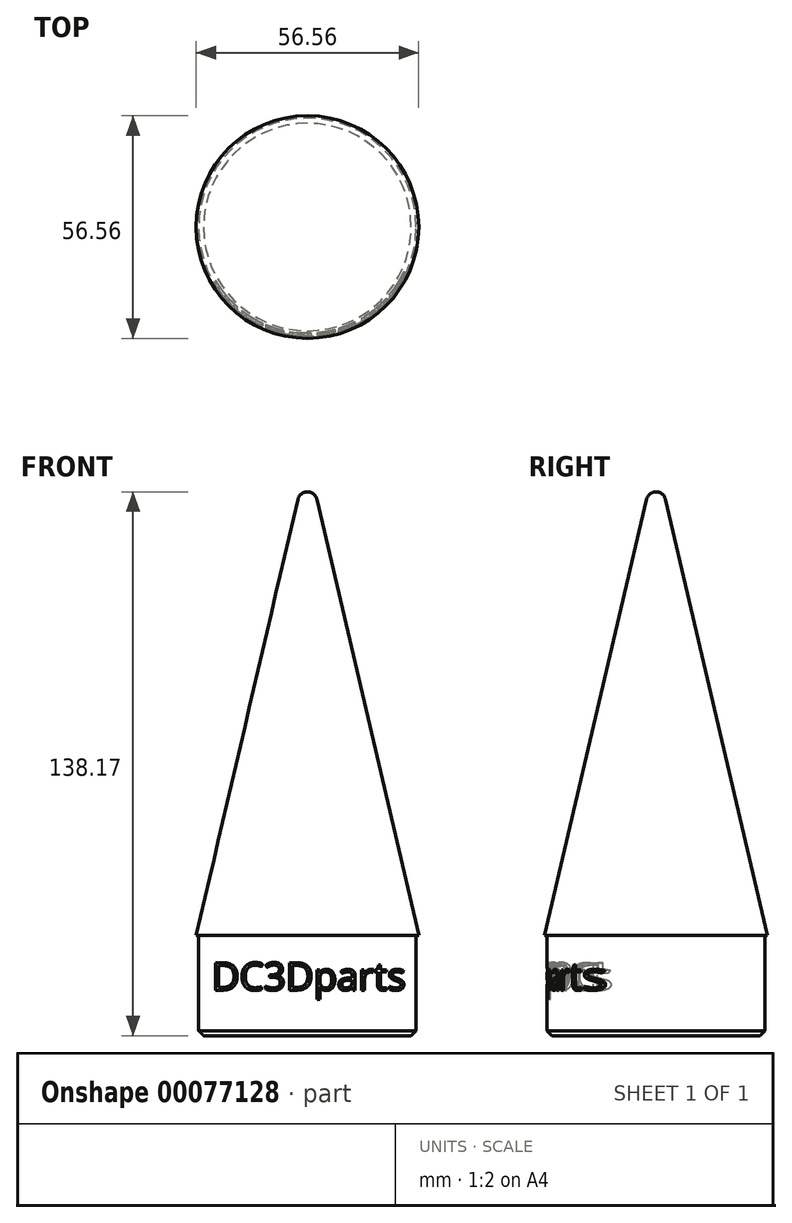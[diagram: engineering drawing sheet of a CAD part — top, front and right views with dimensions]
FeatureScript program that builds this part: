
annotation { "Feature Type Name" : "Feature", "Feature Type Description" : "" }
export const myFeature = defineFeature(function(context is Context, id is Id, definition is map)
    precondition{}
    {
        {
            var Q0;
            Q0=qCreatedBy(makeId("Front.planeOp"),FACE);
            var sketch = newSketch(context, id + "F0", { "sketchPlane" : qUnion([Q0])});
            skLineSegment(sketch, "E0", {"start": v(-33.35, -68.75) * mm, "end": v(-32.6, -68.75) * mm});
            skLineSegment(sketch, "E1", {"start": v(0, -68.75) * mm, "end": v(0, 86.96) * mm});
            skLineSegment(sketch, "E2", {"start": v(0, -68.75) * mm, "end": v(0, -98.75) * mm});
            skLineSegment(sketch, "E3", {"start": v(0, -98.75) * mm, "end": v(-32.6, -98.75) * mm});
            skLineSegment(sketch, "E4", {"start": v(-32.6, -98.75) * mm, "end": v(-32.6, -68.75) * mm});
            skLineSegment(sketch, "E5.trimOffspring", {"start": v(-32.6, -68.75) * mm, "end": v(-33.35, -68.75) * mm});
            skPoint(sketch, "E6.orphan", {"position": v(0, 61.25) * mm});
            skLineSegment(sketch, "E7", {"start": v(-33.35, -68.75) * mm, "end": v(-2.86, 61.92) * mm});
            skArc(sketch, "E8", {"start": v(0, 64.19) * mm, "mid": v(-1.82, 63.55) * mm, "end": v(-2.86, 61.92) * mm});
            skSolve(sketch);
        }
        {
            var Q0;
            {var subQ0=sQuery(id+"F0.wireOp",EDGE,"E2");Q0=makeQuery(id+"F0.imprint","IMPRINT",FACE,{"disambiguationData":[TD([[makeQuery(id+"F0.imprint","IMPRINT",EDGE,{"derivedFrom":subQ0}),-1.0]])]});}
            var Q1;
            Q1=sQuery(id+"F0.wireOp",EDGE,"E1");
            revolve(context, id + "F1", {"entities" : qUnion([Q0]), "axis" : qUnion([Q1]), "revolveType" : RevolveType.FULL});
        }
        {
            var Q0;
            Q0=makeQuery(id+"F1.opRevolve","SWEPT_EDGE",EDGE,{"disambiguationData":[OSD([sQuery(id+"F0.wireOp",EDGE,"E3"),sQuery(id+"F0.wireOp",EDGE,"E4")])]});
            chamfer(context, id + "F2", {"entities" : qUnion([Q0]), "width" : 1.5 * mm, "tangentPropagation" : true});
        }
        {
            var Q0;
            Q0=makeQuery(id+"F1.opRevolve","SWEPT_BODY",BODY,{"disambiguationData":[OSD([sQuery(id+"F0.wireOp",EDGE,"Oh61cgLR-RQo2-T4aV-TcRg-Gp7ijPdUG9jl"),sQuery(id+"F0.wireOp",EDGE,"E1"),sQuery(id+"F0.wireOp",EDGE,"E2"),sQuery(id+"F0.wireOp",EDGE,"E3"),sQuery(id+"F0.wireOp",EDGE,"E4"),sQuery(id+"F0.wireOp",EDGE,"E5.trimOffspring"),sQuery(id+"F0.wireOp",EDGE,"dTV1AxgJ-VMAe-DLQO-Zqz3-4UbtDb8FiUJC")])]});
            var Q1;
            Q1=qCreatedBy(makeId("Origin.pointOp"),VERTEX);
            transform(context, id + "F3", {"entities" : qUnion([Q0]), "transformType" : TransformType.SCALE_UNIFORMLY, "scale" : .848, "scalePoint" : qUnion([Q1]), "makeCopy" : false});
        }
        {
            var Q0;
            Q0=qCreatedBy(makeId("Front.planeOp"),FACE);
            cPlane(context, id + "F4", {"entities" : qUnion([Q0]), "cplaneType" : CPlaneType.OFFSET, "offset" : 35 * mm, "width" : 150 * mm, "height" : 150 * mm});
        }
        {
            var Q0;
            Q0=qCreatedBy(makeId("Front.planeOp"),FACE);
            var sketch = newSketch(context, id + "F5", { "sketchPlane" : qUnion([Q0])});
            skLineSegment(sketch, "E9.bottom", {"start": v(0, -61.28) * mm, "end": v(-27, -61.28) * mm});
            skLineSegment(sketch, "E9.top", {"start": v(0, -97.48) * mm, "end": v(-27, -97.48) * mm});
            skLineSegment(sketch, "E9.left", {"start": v(0, -61.28) * mm, "end": v(0, -97.48) * mm});
            skLineSegment(sketch, "E9.right", {"start": v(-27, -61.28) * mm, "end": v(-27, -97.48) * mm});
            skSolve(sketch);
        }
        {
            var Q0;
            Q0=makeQuery(id+"F5.imprint","IMPRINT",FACE,{"disambiguationData":[TD([[makeQuery(id+"F5.imprint","IMPRINT",EDGE,{"derivedFrom":sQuery(id+"F5.wireOp",EDGE,"E9.bottom")}),1.0]])]});
            var Q1;
            Q1=sQuery(id+"F5.wireOp",EDGE,"E9.left");
            revolve(context, id + "F6", {"entities" : qUnion([Q0]), "axis" : qUnion([Q1]), "revolveType" : RevolveType.FULL});
        }
        {
            var Q0;
            Q0=qCreatedBy(id+"F4.planeOp",FACE);
            var sketch = newSketch(context, id + "F7", { "sketchPlane" : qUnion([Q0])});
            skText(sketch, "E10", { "text": "DC3Dparts", "fontName": "OpenSans-Regular.ttf"});
            const initialGuessF7  = {"E10": [-0.02432, -0.07217, 1, 0, 0.007]};
            skSetInitialGuess(sketch, initialGuessF7);
            skSolve(sketch);
        }
        {
            var Q0;
            Q0 = qSketchRegion(id + "F7", true);
            var Q1;
            Q1=qCreatedBy(makeId("Front.planeOp"),FACE);
            extrude(context, id + "F8", {"entities" : qUnion([Q0]), "endBound" : BoundingType.UP_TO_SURFACE, "oppositeDirection" : true, "depth" : 25 * mm, "endBoundEntityFace" : qUnion([Q1]), "offsetDistance" : 25 * mm});
        }
        {
            var Q0;
            Q0=makeQuery(id+"F6.opRevolve","SWEPT_BODY",BODY,{"disambiguationData":[OSD([sQuery(id+"F5.wireOp",EDGE,"E9.bottom"),sQuery(id+"F5.wireOp",EDGE,"E9.top"),sQuery(id+"F5.wireOp",EDGE,"E9.left"),sQuery(id+"F5.wireOp",EDGE,"E9.right")])]});
            var Q1;
            Q1=makeQuery(id+"F8.opExtrude","SWEPT_BODY",BODY,{"disambiguationData":[OSD([sQuery(id+"F7.wireOp",EDGE,"E10.sketch_text.stroke-0"),sQuery(id+"F7.wireOp",EDGE,"E10.sketch_text.stroke-1"),sQuery(id+"F7.wireOp",EDGE,"E10.sketch_text.stroke-2"),sQuery(id+"F7.wireOp",EDGE,"E10.sketch_text.stroke-3"),sQuery(id+"F7.wireOp",EDGE,"E10.sketch_text.stroke-4"),sQuery(id+"F7.wireOp",EDGE,"E10.sketch_text.stroke-5"),sQuery(id+"F7.wireOp",EDGE,"E10.sketch_text.stroke-6"),sQuery(id+"F7.wireOp",EDGE,"E10.sketch_text.stroke-7"),sQuery(id+"F7.wireOp",EDGE,"E10.sketch_text.stroke-8"),sQuery(id+"F7.wireOp",EDGE,"E10.sketch_text.stroke-9"),sQuery(id+"F7.wireOp",EDGE,"E10.sketch_text.stroke-10"),sQuery(id+"F7.wireOp",EDGE,"E10.sketch_text.stroke-11"),sQuery(id+"F7.wireOp",EDGE,"E10.sketch_text.stroke-12"),sQuery(id+"F7.wireOp",EDGE,"E10.sketch_text.stroke-13")])]});
            var Q2;
            Q2=makeQuery(id+"F8.opExtrude","SWEPT_BODY",BODY,{"disambiguationData":[OSD([sQuery(id+"F7.wireOp",EDGE,"E10.sketch_text.stroke-14"),sQuery(id+"F7.wireOp",EDGE,"E10.sketch_text.stroke-15"),sQuery(id+"F7.wireOp",EDGE,"E10.sketch_text.stroke-16"),sQuery(id+"F7.wireOp",EDGE,"E10.sketch_text.stroke-17"),sQuery(id+"F7.wireOp",EDGE,"E10.sketch_text.stroke-18"),sQuery(id+"F7.wireOp",EDGE,"E10.sketch_text.stroke-19"),sQuery(id+"F7.wireOp",EDGE,"E10.sketch_text.stroke-20"),sQuery(id+"F7.wireOp",EDGE,"E10.sketch_text.stroke-21"),sQuery(id+"F7.wireOp",EDGE,"E10.sketch_text.stroke-22"),sQuery(id+"F7.wireOp",EDGE,"E10.sketch_text.stroke-23"),sQuery(id+"F7.wireOp",EDGE,"E10.sketch_text.stroke-24"),sQuery(id+"F7.wireOp",EDGE,"E10.sketch_text.stroke-25"),sQuery(id+"F7.wireOp",EDGE,"E10.sketch_text.stroke-26"),sQuery(id+"F7.wireOp",EDGE,"E10.sketch_text.stroke-27"),sQuery(id+"F7.wireOp",EDGE,"E10.sketch_text.stroke-28")])]});
            var Q3;
            Q3=makeQuery(id+"F8.opExtrude","SWEPT_BODY",BODY,{"disambiguationData":[OSD([sQuery(id+"F7.wireOp",EDGE,"E10.sketch_text.stroke-29"),sQuery(id+"F7.wireOp",EDGE,"E10.sketch_text.stroke-30"),sQuery(id+"F7.wireOp",EDGE,"E10.sketch_text.stroke-31"),sQuery(id+"F7.wireOp",EDGE,"E10.sketch_text.stroke-32"),sQuery(id+"F7.wireOp",EDGE,"E10.sketch_text.stroke-33"),sQuery(id+"F7.wireOp",EDGE,"E10.sketch_text.stroke-34"),sQuery(id+"F7.wireOp",EDGE,"E10.sketch_text.stroke-35"),sQuery(id+"F7.wireOp",EDGE,"E10.sketch_text.stroke-36"),sQuery(id+"F7.wireOp",EDGE,"E10.sketch_text.stroke-37"),sQuery(id+"F7.wireOp",EDGE,"E10.sketch_text.stroke-38"),sQuery(id+"F7.wireOp",EDGE,"E10.sketch_text.stroke-39"),sQuery(id+"F7.wireOp",EDGE,"E10.sketch_text.stroke-40"),sQuery(id+"F7.wireOp",EDGE,"E10.sketch_text.stroke-41"),sQuery(id+"F7.wireOp",EDGE,"E10.sketch_text.stroke-42"),sQuery(id+"F7.wireOp",EDGE,"E10.sketch_text.stroke-43"),sQuery(id+"F7.wireOp",EDGE,"E10.sketch_text.stroke-44"),sQuery(id+"F7.wireOp",EDGE,"E10.sketch_text.stroke-45"),sQuery(id+"F7.wireOp",EDGE,"E10.sketch_text.stroke-46"),sQuery(id+"F7.wireOp",EDGE,"E10.sketch_text.stroke-47"),sQuery(id+"F7.wireOp",EDGE,"E10.sketch_text.stroke-48"),sQuery(id+"F7.wireOp",EDGE,"E10.sketch_text.stroke-49"),sQuery(id+"F7.wireOp",EDGE,"E10.sketch_text.stroke-50"),sQuery(id+"F7.wireOp",EDGE,"E10.sketch_text.stroke-51"),sQuery(id+"F7.wireOp",EDGE,"E10.sketch_text.stroke-52"),sQuery(id+"F7.wireOp",EDGE,"E10.sketch_text.stroke-53"),sQuery(id+"F7.wireOp",EDGE,"E10.sketch_text.stroke-54"),sQuery(id+"F7.wireOp",EDGE,"E10.sketch_text.stroke-55"),sQuery(id+"F7.wireOp",EDGE,"E10.sketch_text.stroke-56")])]});
            var Q4;
            Q4=makeQuery(id+"F8.opExtrude","SWEPT_BODY",BODY,{"disambiguationData":[OSD([sQuery(id+"F7.wireOp",EDGE,"E10.sketch_text.stroke-57"),sQuery(id+"F7.wireOp",EDGE,"E10.sketch_text.stroke-58"),sQuery(id+"F7.wireOp",EDGE,"E10.sketch_text.stroke-59"),sQuery(id+"F7.wireOp",EDGE,"E10.sketch_text.stroke-60"),sQuery(id+"F7.wireOp",EDGE,"E10.sketch_text.stroke-61"),sQuery(id+"F7.wireOp",EDGE,"E10.sketch_text.stroke-62"),sQuery(id+"F7.wireOp",EDGE,"E10.sketch_text.stroke-63"),sQuery(id+"F7.wireOp",EDGE,"E10.sketch_text.stroke-64"),sQuery(id+"F7.wireOp",EDGE,"E10.sketch_text.stroke-65"),sQuery(id+"F7.wireOp",EDGE,"E10.sketch_text.stroke-66"),sQuery(id+"F7.wireOp",EDGE,"E10.sketch_text.stroke-67"),sQuery(id+"F7.wireOp",EDGE,"E10.sketch_text.stroke-68"),sQuery(id+"F7.wireOp",EDGE,"E10.sketch_text.stroke-69"),sQuery(id+"F7.wireOp",EDGE,"E10.sketch_text.stroke-70")])]});
            var Q5;
            Q5=makeQuery(id+"F8.opExtrude","SWEPT_BODY",BODY,{"disambiguationData":[OSD([sQuery(id+"F7.wireOp",EDGE,"E10.sketch_text.stroke-71"),sQuery(id+"F7.wireOp",EDGE,"E10.sketch_text.stroke-72"),sQuery(id+"F7.wireOp",EDGE,"E10.sketch_text.stroke-73"),sQuery(id+"F7.wireOp",EDGE,"E10.sketch_text.stroke-74"),sQuery(id+"F7.wireOp",EDGE,"E10.sketch_text.stroke-75"),sQuery(id+"F7.wireOp",EDGE,"E10.sketch_text.stroke-76"),sQuery(id+"F7.wireOp",EDGE,"E10.sketch_text.stroke-77"),sQuery(id+"F7.wireOp",EDGE,"E10.sketch_text.stroke-78"),sQuery(id+"F7.wireOp",EDGE,"E10.sketch_text.stroke-79"),sQuery(id+"F7.wireOp",EDGE,"E10.sketch_text.stroke-80"),sQuery(id+"F7.wireOp",EDGE,"E10.sketch_text.stroke-81"),sQuery(id+"F7.wireOp",EDGE,"E10.sketch_text.stroke-82"),sQuery(id+"F7.wireOp",EDGE,"E10.sketch_text.stroke-83"),sQuery(id+"F7.wireOp",EDGE,"E10.sketch_text.stroke-84"),sQuery(id+"F7.wireOp",EDGE,"E10.sketch_text.stroke-85"),sQuery(id+"F7.wireOp",EDGE,"E10.sketch_text.stroke-86"),sQuery(id+"F7.wireOp",EDGE,"E10.sketch_text.stroke-87"),sQuery(id+"F7.wireOp",EDGE,"E10.sketch_text.stroke-88"),sQuery(id+"F7.wireOp",EDGE,"E10.sketch_text.stroke-89"),sQuery(id+"F7.wireOp",EDGE,"E10.sketch_text.stroke-90"),sQuery(id+"F7.wireOp",EDGE,"E10.sketch_text.stroke-91"),sQuery(id+"F7.wireOp",EDGE,"E10.sketch_text.stroke-92"),sQuery(id+"F7.wireOp",EDGE,"E10.sketch_text.stroke-93"),sQuery(id+"F7.wireOp",EDGE,"E10.sketch_text.stroke-94"),sQuery(id+"F7.wireOp",EDGE,"E10.sketch_text.stroke-95")])]});
            var Q6;
            Q6=makeQuery(id+"F8.opExtrude","SWEPT_BODY",BODY,{"disambiguationData":[OSD([sQuery(id+"F7.wireOp",EDGE,"E10.sketch_text.stroke-96"),sQuery(id+"F7.wireOp",EDGE,"E10.sketch_text.stroke-97"),sQuery(id+"F7.wireOp",EDGE,"E10.sketch_text.stroke-98"),sQuery(id+"F7.wireOp",EDGE,"E10.sketch_text.stroke-99"),sQuery(id+"F7.wireOp",EDGE,"E10.sketch_text.stroke-100"),sQuery(id+"F7.wireOp",EDGE,"E10.sketch_text.stroke-101"),sQuery(id+"F7.wireOp",EDGE,"E10.sketch_text.stroke-102"),sQuery(id+"F7.wireOp",EDGE,"E10.sketch_text.stroke-103"),sQuery(id+"F7.wireOp",EDGE,"E10.sketch_text.stroke-104"),sQuery(id+"F7.wireOp",EDGE,"E10.sketch_text.stroke-105"),sQuery(id+"F7.wireOp",EDGE,"E10.sketch_text.stroke-106"),sQuery(id+"F7.wireOp",EDGE,"E10.sketch_text.stroke-107"),sQuery(id+"F7.wireOp",EDGE,"E10.sketch_text.stroke-108"),sQuery(id+"F7.wireOp",EDGE,"E10.sketch_text.stroke-109"),sQuery(id+"F7.wireOp",EDGE,"E10.sketch_text.stroke-110"),sQuery(id+"F7.wireOp",EDGE,"E10.sketch_text.stroke-111"),sQuery(id+"F7.wireOp",EDGE,"E10.sketch_text.stroke-112"),sQuery(id+"F7.wireOp",EDGE,"E10.sketch_text.stroke-113"),sQuery(id+"F7.wireOp",EDGE,"E10.sketch_text.stroke-114"),sQuery(id+"F7.wireOp",EDGE,"E10.sketch_text.stroke-115"),sQuery(id+"F7.wireOp",EDGE,"E10.sketch_text.stroke-116"),sQuery(id+"F7.wireOp",EDGE,"E10.sketch_text.stroke-117"),sQuery(id+"F7.wireOp",EDGE,"E10.sketch_text.stroke-118"),sQuery(id+"F7.wireOp",EDGE,"E10.sketch_text.stroke-119"),sQuery(id+"F7.wireOp",EDGE,"E10.sketch_text.stroke-120"),sQuery(id+"F7.wireOp",EDGE,"E10.sketch_text.stroke-121"),sQuery(id+"F7.wireOp",EDGE,"E10.sketch_text.stroke-122")])]});
            var Q7;
            Q7=makeQuery(id+"F8.opExtrude","SWEPT_BODY",BODY,{"disambiguationData":[OSD([sQuery(id+"F7.wireOp",EDGE,"E10.sketch_text.stroke-123"),sQuery(id+"F7.wireOp",EDGE,"E10.sketch_text.stroke-124"),sQuery(id+"F7.wireOp",EDGE,"E10.sketch_text.stroke-125"),sQuery(id+"F7.wireOp",EDGE,"E10.sketch_text.stroke-126"),sQuery(id+"F7.wireOp",EDGE,"E10.sketch_text.stroke-127"),sQuery(id+"F7.wireOp",EDGE,"E10.sketch_text.stroke-128"),sQuery(id+"F7.wireOp",EDGE,"E10.sketch_text.stroke-129"),sQuery(id+"F7.wireOp",EDGE,"E10.sketch_text.stroke-130"),sQuery(id+"F7.wireOp",EDGE,"E10.sketch_text.stroke-131"),sQuery(id+"F7.wireOp",EDGE,"E10.sketch_text.stroke-132"),sQuery(id+"F7.wireOp",EDGE,"E10.sketch_text.stroke-133"),sQuery(id+"F7.wireOp",EDGE,"E10.sketch_text.stroke-134"),sQuery(id+"F7.wireOp",EDGE,"E10.sketch_text.stroke-135")])]});
            var Q8;
            Q8=makeQuery(id+"F8.opExtrude","SWEPT_BODY",BODY,{"disambiguationData":[OSD([sQuery(id+"F7.wireOp",EDGE,"E10.sketch_text.stroke-136"),sQuery(id+"F7.wireOp",EDGE,"E10.sketch_text.stroke-137"),sQuery(id+"F7.wireOp",EDGE,"E10.sketch_text.stroke-138"),sQuery(id+"F7.wireOp",EDGE,"E10.sketch_text.stroke-139"),sQuery(id+"F7.wireOp",EDGE,"E10.sketch_text.stroke-140"),sQuery(id+"F7.wireOp",EDGE,"E10.sketch_text.stroke-141"),sQuery(id+"F7.wireOp",EDGE,"E10.sketch_text.stroke-142"),sQuery(id+"F7.wireOp",EDGE,"E10.sketch_text.stroke-143"),sQuery(id+"F7.wireOp",EDGE,"E10.sketch_text.stroke-144"),sQuery(id+"F7.wireOp",EDGE,"E10.sketch_text.stroke-145"),sQuery(id+"F7.wireOp",EDGE,"E10.sketch_text.stroke-146"),sQuery(id+"F7.wireOp",EDGE,"E10.sketch_text.stroke-147"),sQuery(id+"F7.wireOp",EDGE,"E10.sketch_text.stroke-148"),sQuery(id+"F7.wireOp",EDGE,"E10.sketch_text.stroke-149"),sQuery(id+"F7.wireOp",EDGE,"E10.sketch_text.stroke-150"),sQuery(id+"F7.wireOp",EDGE,"E10.sketch_text.stroke-151"),sQuery(id+"F7.wireOp",EDGE,"E10.sketch_text.stroke-152"),sQuery(id+"F7.wireOp",EDGE,"E10.sketch_text.stroke-153"),sQuery(id+"F7.wireOp",EDGE,"E10.sketch_text.stroke-154")])]});
            var Q9;
            Q9=makeQuery(id+"F8.opExtrude","SWEPT_BODY",BODY,{"disambiguationData":[OSD([sQuery(id+"F7.wireOp",EDGE,"E10.sketch_text.stroke-155"),sQuery(id+"F7.wireOp",EDGE,"E10.sketch_text.stroke-156"),sQuery(id+"F7.wireOp",EDGE,"E10.sketch_text.stroke-157"),sQuery(id+"F7.wireOp",EDGE,"E10.sketch_text.stroke-158"),sQuery(id+"F7.wireOp",EDGE,"E10.sketch_text.stroke-159"),sQuery(id+"F7.wireOp",EDGE,"E10.sketch_text.stroke-160"),sQuery(id+"F7.wireOp",EDGE,"E10.sketch_text.stroke-161"),sQuery(id+"F7.wireOp",EDGE,"E10.sketch_text.stroke-162"),sQuery(id+"F7.wireOp",EDGE,"E10.sketch_text.stroke-163"),sQuery(id+"F7.wireOp",EDGE,"E10.sketch_text.stroke-164"),sQuery(id+"F7.wireOp",EDGE,"E10.sketch_text.stroke-165"),sQuery(id+"F7.wireOp",EDGE,"E10.sketch_text.stroke-166"),sQuery(id+"F7.wireOp",EDGE,"E10.sketch_text.stroke-167"),sQuery(id+"F7.wireOp",EDGE,"E10.sketch_text.stroke-168"),sQuery(id+"F7.wireOp",EDGE,"E10.sketch_text.stroke-169"),sQuery(id+"F7.wireOp",EDGE,"E10.sketch_text.stroke-170"),sQuery(id+"F7.wireOp",EDGE,"E10.sketch_text.stroke-171"),sQuery(id+"F7.wireOp",EDGE,"E10.sketch_text.stroke-172"),sQuery(id+"F7.wireOp",EDGE,"E10.sketch_text.stroke-173"),sQuery(id+"F7.wireOp",EDGE,"E10.sketch_text.stroke-174"),sQuery(id+"F7.wireOp",EDGE,"E10.sketch_text.stroke-175"),sQuery(id+"F7.wireOp",EDGE,"E10.sketch_text.stroke-176"),sQuery(id+"F7.wireOp",EDGE,"E10.sketch_text.stroke-177"),sQuery(id+"F7.wireOp",EDGE,"E10.sketch_text.stroke-178"),sQuery(id+"F7.wireOp",EDGE,"E10.sketch_text.stroke-179")])]});
            booleanBodies(context, id + "F9", {"operationType" : BooleanOperationType.SUBTRACTION, "tools" : qUnion([Q0]), "targets" : qUnion([Q1, Q2, Q3, Q4, Q5, Q6, Q7, Q8, Q9])});
        }
        {
            var Q0;
            Q0=makeQuery(id+"F8.opExtrude","SWEPT_BODY",BODY,{"disambiguationData":[OSD([sQuery(id+"F7.wireOp",EDGE,"E10.sketch_text.stroke-0"),sQuery(id+"F7.wireOp",EDGE,"E10.sketch_text.stroke-1"),sQuery(id+"F7.wireOp",EDGE,"E10.sketch_text.stroke-2"),sQuery(id+"F7.wireOp",EDGE,"E10.sketch_text.stroke-3"),sQuery(id+"F7.wireOp",EDGE,"E10.sketch_text.stroke-4"),sQuery(id+"F7.wireOp",EDGE,"E10.sketch_text.stroke-5"),sQuery(id+"F7.wireOp",EDGE,"E10.sketch_text.stroke-6"),sQuery(id+"F7.wireOp",EDGE,"E10.sketch_text.stroke-7"),sQuery(id+"F7.wireOp",EDGE,"E10.sketch_text.stroke-8"),sQuery(id+"F7.wireOp",EDGE,"E10.sketch_text.stroke-9"),sQuery(id+"F7.wireOp",EDGE,"E10.sketch_text.stroke-10"),sQuery(id+"F7.wireOp",EDGE,"E10.sketch_text.stroke-11"),sQuery(id+"F7.wireOp",EDGE,"E10.sketch_text.stroke-12"),sQuery(id+"F7.wireOp",EDGE,"E10.sketch_text.stroke-13")])]});
            var Q1;
            Q1=makeQuery(id+"F8.opExtrude","SWEPT_BODY",BODY,{"disambiguationData":[OSD([sQuery(id+"F7.wireOp",EDGE,"E10.sketch_text.stroke-14"),sQuery(id+"F7.wireOp",EDGE,"E10.sketch_text.stroke-15"),sQuery(id+"F7.wireOp",EDGE,"E10.sketch_text.stroke-16"),sQuery(id+"F7.wireOp",EDGE,"E10.sketch_text.stroke-17"),sQuery(id+"F7.wireOp",EDGE,"E10.sketch_text.stroke-18"),sQuery(id+"F7.wireOp",EDGE,"E10.sketch_text.stroke-19"),sQuery(id+"F7.wireOp",EDGE,"E10.sketch_text.stroke-20"),sQuery(id+"F7.wireOp",EDGE,"E10.sketch_text.stroke-21"),sQuery(id+"F7.wireOp",EDGE,"E10.sketch_text.stroke-22"),sQuery(id+"F7.wireOp",EDGE,"E10.sketch_text.stroke-23"),sQuery(id+"F7.wireOp",EDGE,"E10.sketch_text.stroke-24"),sQuery(id+"F7.wireOp",EDGE,"E10.sketch_text.stroke-25"),sQuery(id+"F7.wireOp",EDGE,"E10.sketch_text.stroke-26"),sQuery(id+"F7.wireOp",EDGE,"E10.sketch_text.stroke-27"),sQuery(id+"F7.wireOp",EDGE,"E10.sketch_text.stroke-28")])]});
            var Q2;
            Q2=makeQuery(id+"F8.opExtrude","SWEPT_BODY",BODY,{"disambiguationData":[OSD([sQuery(id+"F7.wireOp",EDGE,"E10.sketch_text.stroke-29"),sQuery(id+"F7.wireOp",EDGE,"E10.sketch_text.stroke-30"),sQuery(id+"F7.wireOp",EDGE,"E10.sketch_text.stroke-31"),sQuery(id+"F7.wireOp",EDGE,"E10.sketch_text.stroke-32"),sQuery(id+"F7.wireOp",EDGE,"E10.sketch_text.stroke-33"),sQuery(id+"F7.wireOp",EDGE,"E10.sketch_text.stroke-34"),sQuery(id+"F7.wireOp",EDGE,"E10.sketch_text.stroke-35"),sQuery(id+"F7.wireOp",EDGE,"E10.sketch_text.stroke-36"),sQuery(id+"F7.wireOp",EDGE,"E10.sketch_text.stroke-37"),sQuery(id+"F7.wireOp",EDGE,"E10.sketch_text.stroke-38"),sQuery(id+"F7.wireOp",EDGE,"E10.sketch_text.stroke-39"),sQuery(id+"F7.wireOp",EDGE,"E10.sketch_text.stroke-40"),sQuery(id+"F7.wireOp",EDGE,"E10.sketch_text.stroke-41"),sQuery(id+"F7.wireOp",EDGE,"E10.sketch_text.stroke-42"),sQuery(id+"F7.wireOp",EDGE,"E10.sketch_text.stroke-43"),sQuery(id+"F7.wireOp",EDGE,"E10.sketch_text.stroke-44"),sQuery(id+"F7.wireOp",EDGE,"E10.sketch_text.stroke-45"),sQuery(id+"F7.wireOp",EDGE,"E10.sketch_text.stroke-46"),sQuery(id+"F7.wireOp",EDGE,"E10.sketch_text.stroke-47"),sQuery(id+"F7.wireOp",EDGE,"E10.sketch_text.stroke-48"),sQuery(id+"F7.wireOp",EDGE,"E10.sketch_text.stroke-49"),sQuery(id+"F7.wireOp",EDGE,"E10.sketch_text.stroke-50"),sQuery(id+"F7.wireOp",EDGE,"E10.sketch_text.stroke-51"),sQuery(id+"F7.wireOp",EDGE,"E10.sketch_text.stroke-52"),sQuery(id+"F7.wireOp",EDGE,"E10.sketch_text.stroke-53"),sQuery(id+"F7.wireOp",EDGE,"E10.sketch_text.stroke-54"),sQuery(id+"F7.wireOp",EDGE,"E10.sketch_text.stroke-55"),sQuery(id+"F7.wireOp",EDGE,"E10.sketch_text.stroke-56")])]});
            var Q3;
            Q3=makeQuery(id+"F8.opExtrude","SWEPT_BODY",BODY,{"disambiguationData":[OSD([sQuery(id+"F7.wireOp",EDGE,"E10.sketch_text.stroke-57"),sQuery(id+"F7.wireOp",EDGE,"E10.sketch_text.stroke-58"),sQuery(id+"F7.wireOp",EDGE,"E10.sketch_text.stroke-59"),sQuery(id+"F7.wireOp",EDGE,"E10.sketch_text.stroke-60"),sQuery(id+"F7.wireOp",EDGE,"E10.sketch_text.stroke-61"),sQuery(id+"F7.wireOp",EDGE,"E10.sketch_text.stroke-62"),sQuery(id+"F7.wireOp",EDGE,"E10.sketch_text.stroke-63"),sQuery(id+"F7.wireOp",EDGE,"E10.sketch_text.stroke-64"),sQuery(id+"F7.wireOp",EDGE,"E10.sketch_text.stroke-65"),sQuery(id+"F7.wireOp",EDGE,"E10.sketch_text.stroke-66"),sQuery(id+"F7.wireOp",EDGE,"E10.sketch_text.stroke-67"),sQuery(id+"F7.wireOp",EDGE,"E10.sketch_text.stroke-68"),sQuery(id+"F7.wireOp",EDGE,"E10.sketch_text.stroke-69"),sQuery(id+"F7.wireOp",EDGE,"E10.sketch_text.stroke-70")])]});
            var Q4;
            Q4=makeQuery(id+"F8.opExtrude","SWEPT_BODY",BODY,{"disambiguationData":[OSD([sQuery(id+"F7.wireOp",EDGE,"E10.sketch_text.stroke-71"),sQuery(id+"F7.wireOp",EDGE,"E10.sketch_text.stroke-72"),sQuery(id+"F7.wireOp",EDGE,"E10.sketch_text.stroke-73"),sQuery(id+"F7.wireOp",EDGE,"E10.sketch_text.stroke-74"),sQuery(id+"F7.wireOp",EDGE,"E10.sketch_text.stroke-75"),sQuery(id+"F7.wireOp",EDGE,"E10.sketch_text.stroke-76"),sQuery(id+"F7.wireOp",EDGE,"E10.sketch_text.stroke-77"),sQuery(id+"F7.wireOp",EDGE,"E10.sketch_text.stroke-78"),sQuery(id+"F7.wireOp",EDGE,"E10.sketch_text.stroke-79"),sQuery(id+"F7.wireOp",EDGE,"E10.sketch_text.stroke-80"),sQuery(id+"F7.wireOp",EDGE,"E10.sketch_text.stroke-81"),sQuery(id+"F7.wireOp",EDGE,"E10.sketch_text.stroke-82"),sQuery(id+"F7.wireOp",EDGE,"E10.sketch_text.stroke-83"),sQuery(id+"F7.wireOp",EDGE,"E10.sketch_text.stroke-84"),sQuery(id+"F7.wireOp",EDGE,"E10.sketch_text.stroke-85"),sQuery(id+"F7.wireOp",EDGE,"E10.sketch_text.stroke-86"),sQuery(id+"F7.wireOp",EDGE,"E10.sketch_text.stroke-87"),sQuery(id+"F7.wireOp",EDGE,"E10.sketch_text.stroke-88"),sQuery(id+"F7.wireOp",EDGE,"E10.sketch_text.stroke-89"),sQuery(id+"F7.wireOp",EDGE,"E10.sketch_text.stroke-90"),sQuery(id+"F7.wireOp",EDGE,"E10.sketch_text.stroke-91"),sQuery(id+"F7.wireOp",EDGE,"E10.sketch_text.stroke-92"),sQuery(id+"F7.wireOp",EDGE,"E10.sketch_text.stroke-93"),sQuery(id+"F7.wireOp",EDGE,"E10.sketch_text.stroke-94"),sQuery(id+"F7.wireOp",EDGE,"E10.sketch_text.stroke-95")])]});
            var Q5;
            Q5=makeQuery(id+"F8.opExtrude","SWEPT_BODY",BODY,{"disambiguationData":[OSD([sQuery(id+"F7.wireOp",EDGE,"E10.sketch_text.stroke-96"),sQuery(id+"F7.wireOp",EDGE,"E10.sketch_text.stroke-97"),sQuery(id+"F7.wireOp",EDGE,"E10.sketch_text.stroke-98"),sQuery(id+"F7.wireOp",EDGE,"E10.sketch_text.stroke-99"),sQuery(id+"F7.wireOp",EDGE,"E10.sketch_text.stroke-100"),sQuery(id+"F7.wireOp",EDGE,"E10.sketch_text.stroke-101"),sQuery(id+"F7.wireOp",EDGE,"E10.sketch_text.stroke-102"),sQuery(id+"F7.wireOp",EDGE,"E10.sketch_text.stroke-103"),sQuery(id+"F7.wireOp",EDGE,"E10.sketch_text.stroke-104"),sQuery(id+"F7.wireOp",EDGE,"E10.sketch_text.stroke-105"),sQuery(id+"F7.wireOp",EDGE,"E10.sketch_text.stroke-106"),sQuery(id+"F7.wireOp",EDGE,"E10.sketch_text.stroke-107"),sQuery(id+"F7.wireOp",EDGE,"E10.sketch_text.stroke-108"),sQuery(id+"F7.wireOp",EDGE,"E10.sketch_text.stroke-109"),sQuery(id+"F7.wireOp",EDGE,"E10.sketch_text.stroke-110"),sQuery(id+"F7.wireOp",EDGE,"E10.sketch_text.stroke-111"),sQuery(id+"F7.wireOp",EDGE,"E10.sketch_text.stroke-112"),sQuery(id+"F7.wireOp",EDGE,"E10.sketch_text.stroke-113"),sQuery(id+"F7.wireOp",EDGE,"E10.sketch_text.stroke-114"),sQuery(id+"F7.wireOp",EDGE,"E10.sketch_text.stroke-115"),sQuery(id+"F7.wireOp",EDGE,"E10.sketch_text.stroke-116"),sQuery(id+"F7.wireOp",EDGE,"E10.sketch_text.stroke-117"),sQuery(id+"F7.wireOp",EDGE,"E10.sketch_text.stroke-118"),sQuery(id+"F7.wireOp",EDGE,"E10.sketch_text.stroke-119"),sQuery(id+"F7.wireOp",EDGE,"E10.sketch_text.stroke-120"),sQuery(id+"F7.wireOp",EDGE,"E10.sketch_text.stroke-121"),sQuery(id+"F7.wireOp",EDGE,"E10.sketch_text.stroke-122")])]});
            var Q6;
            Q6=makeQuery(id+"F8.opExtrude","SWEPT_BODY",BODY,{"disambiguationData":[OSD([sQuery(id+"F7.wireOp",EDGE,"E10.sketch_text.stroke-123"),sQuery(id+"F7.wireOp",EDGE,"E10.sketch_text.stroke-124"),sQuery(id+"F7.wireOp",EDGE,"E10.sketch_text.stroke-125"),sQuery(id+"F7.wireOp",EDGE,"E10.sketch_text.stroke-126"),sQuery(id+"F7.wireOp",EDGE,"E10.sketch_text.stroke-127"),sQuery(id+"F7.wireOp",EDGE,"E10.sketch_text.stroke-128"),sQuery(id+"F7.wireOp",EDGE,"E10.sketch_text.stroke-129"),sQuery(id+"F7.wireOp",EDGE,"E10.sketch_text.stroke-130"),sQuery(id+"F7.wireOp",EDGE,"E10.sketch_text.stroke-131"),sQuery(id+"F7.wireOp",EDGE,"E10.sketch_text.stroke-132"),sQuery(id+"F7.wireOp",EDGE,"E10.sketch_text.stroke-133"),sQuery(id+"F7.wireOp",EDGE,"E10.sketch_text.stroke-134"),sQuery(id+"F7.wireOp",EDGE,"E10.sketch_text.stroke-135")])]});
            var Q7;
            Q7=makeQuery(id+"F8.opExtrude","SWEPT_BODY",BODY,{"disambiguationData":[OSD([sQuery(id+"F7.wireOp",EDGE,"E10.sketch_text.stroke-136"),sQuery(id+"F7.wireOp",EDGE,"E10.sketch_text.stroke-137"),sQuery(id+"F7.wireOp",EDGE,"E10.sketch_text.stroke-138"),sQuery(id+"F7.wireOp",EDGE,"E10.sketch_text.stroke-139"),sQuery(id+"F7.wireOp",EDGE,"E10.sketch_text.stroke-140"),sQuery(id+"F7.wireOp",EDGE,"E10.sketch_text.stroke-141"),sQuery(id+"F7.wireOp",EDGE,"E10.sketch_text.stroke-142"),sQuery(id+"F7.wireOp",EDGE,"E10.sketch_text.stroke-143"),sQuery(id+"F7.wireOp",EDGE,"E10.sketch_text.stroke-144"),sQuery(id+"F7.wireOp",EDGE,"E10.sketch_text.stroke-145"),sQuery(id+"F7.wireOp",EDGE,"E10.sketch_text.stroke-146"),sQuery(id+"F7.wireOp",EDGE,"E10.sketch_text.stroke-147"),sQuery(id+"F7.wireOp",EDGE,"E10.sketch_text.stroke-148"),sQuery(id+"F7.wireOp",EDGE,"E10.sketch_text.stroke-149"),sQuery(id+"F7.wireOp",EDGE,"E10.sketch_text.stroke-150"),sQuery(id+"F7.wireOp",EDGE,"E10.sketch_text.stroke-151"),sQuery(id+"F7.wireOp",EDGE,"E10.sketch_text.stroke-152"),sQuery(id+"F7.wireOp",EDGE,"E10.sketch_text.stroke-153"),sQuery(id+"F7.wireOp",EDGE,"E10.sketch_text.stroke-154")])]});
            var Q8;
            Q8=makeQuery(id+"F8.opExtrude","SWEPT_BODY",BODY,{"disambiguationData":[OSD([sQuery(id+"F7.wireOp",EDGE,"E10.sketch_text.stroke-155"),sQuery(id+"F7.wireOp",EDGE,"E10.sketch_text.stroke-156"),sQuery(id+"F7.wireOp",EDGE,"E10.sketch_text.stroke-157"),sQuery(id+"F7.wireOp",EDGE,"E10.sketch_text.stroke-158"),sQuery(id+"F7.wireOp",EDGE,"E10.sketch_text.stroke-159"),sQuery(id+"F7.wireOp",EDGE,"E10.sketch_text.stroke-160"),sQuery(id+"F7.wireOp",EDGE,"E10.sketch_text.stroke-161"),sQuery(id+"F7.wireOp",EDGE,"E10.sketch_text.stroke-162"),sQuery(id+"F7.wireOp",EDGE,"E10.sketch_text.stroke-163"),sQuery(id+"F7.wireOp",EDGE,"E10.sketch_text.stroke-164"),sQuery(id+"F7.wireOp",EDGE,"E10.sketch_text.stroke-165"),sQuery(id+"F7.wireOp",EDGE,"E10.sketch_text.stroke-166"),sQuery(id+"F7.wireOp",EDGE,"E10.sketch_text.stroke-167"),sQuery(id+"F7.wireOp",EDGE,"E10.sketch_text.stroke-168"),sQuery(id+"F7.wireOp",EDGE,"E10.sketch_text.stroke-169"),sQuery(id+"F7.wireOp",EDGE,"E10.sketch_text.stroke-170"),sQuery(id+"F7.wireOp",EDGE,"E10.sketch_text.stroke-171"),sQuery(id+"F7.wireOp",EDGE,"E10.sketch_text.stroke-172"),sQuery(id+"F7.wireOp",EDGE,"E10.sketch_text.stroke-173"),sQuery(id+"F7.wireOp",EDGE,"E10.sketch_text.stroke-174"),sQuery(id+"F7.wireOp",EDGE,"E10.sketch_text.stroke-175"),sQuery(id+"F7.wireOp",EDGE,"E10.sketch_text.stroke-176"),sQuery(id+"F7.wireOp",EDGE,"E10.sketch_text.stroke-177"),sQuery(id+"F7.wireOp",EDGE,"E10.sketch_text.stroke-178"),sQuery(id+"F7.wireOp",EDGE,"E10.sketch_text.stroke-179")])]});
            var Q9;
            Q9=makeQuery(id+"F1.opRevolve","SWEPT_BODY",BODY,{"disambiguationData":[OSD([sQuery(id+"F0.wireOp",EDGE,"E1"),sQuery(id+"F0.wireOp",EDGE,"E2"),sQuery(id+"F0.wireOp",EDGE,"E3"),sQuery(id+"F0.wireOp",EDGE,"E4"),sQuery(id+"F0.wireOp",EDGE,"E5.trimOffspring"),sQuery(id+"F0.wireOp",EDGE,"E7"),sQuery(id+"F0.wireOp",EDGE,"E8")])]});
            booleanBodies(context, id + "F10", {"operationType" : BooleanOperationType.SUBTRACTION, "tools" : qUnion([Q0, Q1, Q2, Q3, Q4, Q5, Q6, Q7, Q8]), "targets" : qUnion([Q9])});
        }
    });
